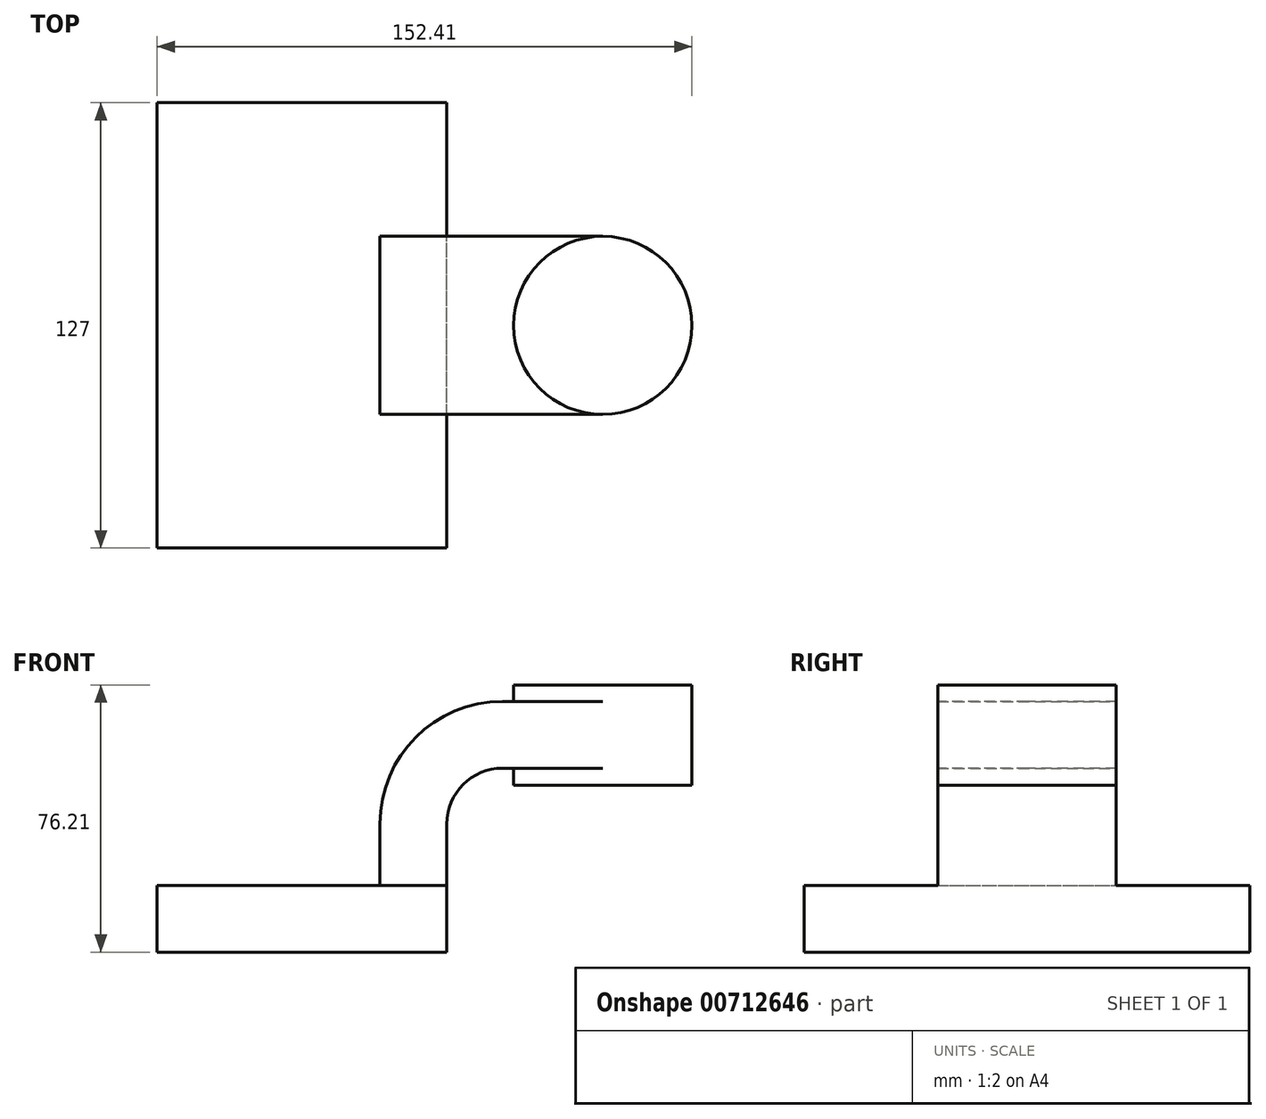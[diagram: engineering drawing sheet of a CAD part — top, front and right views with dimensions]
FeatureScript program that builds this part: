
annotation { "Feature Type Name" : "Feature", "Feature Type Description" : "" }
export const myFeature = defineFeature(function(context is Context, id is Id, definition is map)
    precondition{}
    {
        {
            var Q0;
            Q0=qCreatedBy(makeId("Front.planeOp"),FACE);
            var sketch = newSketch(context, id + "F0", { "sketchPlane" : qUnion([Q0])});
            skLineSegment(sketch, "E0.bottom", {"start": v(-41.28, -9.52) * mm, "end": v(41.28, -9.52) * mm});
            skLineSegment(sketch, "E0.top", {"start": v(-41.28, 9.52) * mm, "end": v(41.27, 9.52) * mm});
            skLineSegment(sketch, "E0.left", {"start": v(-41.27, -9.52) * mm, "end": v(-41.28, 9.52) * mm});
            skLineSegment(sketch, "E0.right", {"start": v(41.28, -9.52) * mm, "end": v(41.27, 9.52) * mm});
            skPoint(sketch, "E0.middle", {"position": v(0, 0) * mm});
            skLineSegment(sketch, "E1.bottom", {"start": v(60.32, 38.1) * mm, "end": v(111.12, 38.1) * mm});
            skLineSegment(sketch, "E1.top", {"start": v(60.32, 66.68) * mm, "end": v(111.12, 66.68) * mm});
            skLineSegment(sketch, "E1.left", {"start": v(60.32, 38.1) * mm, "end": v(60.32, 66.68) * mm});
            skLineSegment(sketch, "E1.right", {"start": v(111.12, 38.1) * mm, "end": v(111.12, 66.68) * mm});
            skPoint(sketch, "E1.middle", {"position": v(85.72, 52.39) * mm});
            skLineSegment(sketch, "E2", {"start": v(41.27, 9.52) * mm, "end": v(41.27, 27.05) * mm});
            skArc(sketch, "E3", {"start": v(41.27, 27.05) * mm, "mid": v(45.92, 38.28) * mm, "end": v(57.15, 42.93) * mm});
            skLineSegment(sketch, "E4", {"start": v(57.15, 42.93) * mm, "end": v(85.73, 42.93) * mm});
            skLineSegment(sketch, "E5.0", {"start": v(57.15, 61.98) * mm, "end": v(85.73, 61.98) * mm});
            skArc(sketch, "E5.1", {"start": v(22.23, 27.05) * mm, "mid": v(32.45, 51.75) * mm, "end": v(57.15, 61.98) * mm});
            skLineSegment(sketch, "E5.2", {"start": v(22.22, 9.52) * mm, "end": v(22.22, 27.05) * mm});
            skLineSegment(sketch, "E6", {"start": v(85.72, 38.1) * mm, "end": v(85.72, 66.68) * mm});
            skFitSpline(sketch, "E7", {"points": [v(-41.28, 9.53) * mm, v(57.15, 61.98) * mm], "startDerivative": vector(-1.7, 84.72) * mm, "endDerivative": vector(213.92, -0.93) * mm});
            skSolve(sketch);
        }
        {
            var Q0;
            Q0=makeQuery(id+"F0.imprint","IMPRINT",FACE,{"disambiguationData":[TD([[makeQuery(id+"F0.imprint","IMPRINT",EDGE,{"derivedFrom":sQuery(id+"F0.wireOp",EDGE,"E0.bottom")}),1.0]])]});
            extrude(context, id + "F1", {"entities" : qUnion([Q0]), "endBound" : BoundingType.SYMMETRIC, "depth" : 127 * mm, "offsetDistance" : 25.4 * mm});
        }
        {
            var Q0;
            {var subQ1=sQuery(id+"F0.wireOp",EDGE,"E2");Q0=makeQuery(id+"F0.imprint","IMPRINT",FACE,{"disambiguationData":[TD([[makeQuery(id+"F0.imprint","IMPRINT",EDGE,{"derivedFrom":subQ1}),1.0]])]});}
            var Q1;
            {var subQ0=sQuery(id+"F0.wireOp",EDGE,"E4");var subQ1=sQuery(id+"F0.wireOp",EDGE,"E1.left");var subQ2=makeQuery(id+"F0.imprint","INTERSECT",VERTEX,{"derivedFrom":[subQ1,subQ0]});Q1=makeQuery(id+"F0.imprint","IMPRINT",FACE,{"disambiguationData":[TD([[makeQuery(id+"F0.imprint","IMPRINT",EDGE,{"disambiguationData":[TD([[subQ2,-1.0]])],"derivedFrom":subQ1}),-1.0]])]});}
            extrude(context, id + "F2", {"entities" : qUnion([Q0, Q1]), "operationType" : NewBodyOperationType.ADD, "endBound" : BoundingType.SYMMETRIC, "depth" : 50.8 * mm, "offsetDistance" : 25.4 * mm});
        }
        {
            var Q0;
            Q0=makeQuery(id+"F0.imprint","IMPRINT",FACE,{"disambiguationData":[TD([[makeQuery(id+"F0.imprint","IMPRINT",EDGE,{"derivedFrom":sQuery(id+"F0.wireOp",EDGE,"E5.1")}),1.0]])]});
            extrude(context, id + "F3", {"entities" : qUnion([Q0]), "operationType" : NewBodyOperationType.ADD, "endBound" : BoundingType.SYMMETRIC, "depth" : 15.88 * mm, "offsetDistance" : 25.4 * mm});
        }
        {
            var Q0;
            {var subQ0=sQuery(id+"F0.wireOp",EDGE,"E1.right");Q0=makeQuery(id+"F0.imprint","IMPRINT",FACE,{"disambiguationData":[TD([[makeQuery(id+"F0.imprint","IMPRINT",EDGE,{"derivedFrom":subQ0}),1.0]])]});}
            var Q1;
            Q1=sQuery(id+"F0.wireOp",EDGE,"E6");
            revolve(context, id + "F4", {"operationType" : NewBodyOperationType.ADD, "surfaceOperationType" : NewSurfaceOperationType.NEW, "entities" : qUnion([Q0]), "axis" : qUnion([Q1]), "revolveType" : RevolveType.FULL});
        }
    });
